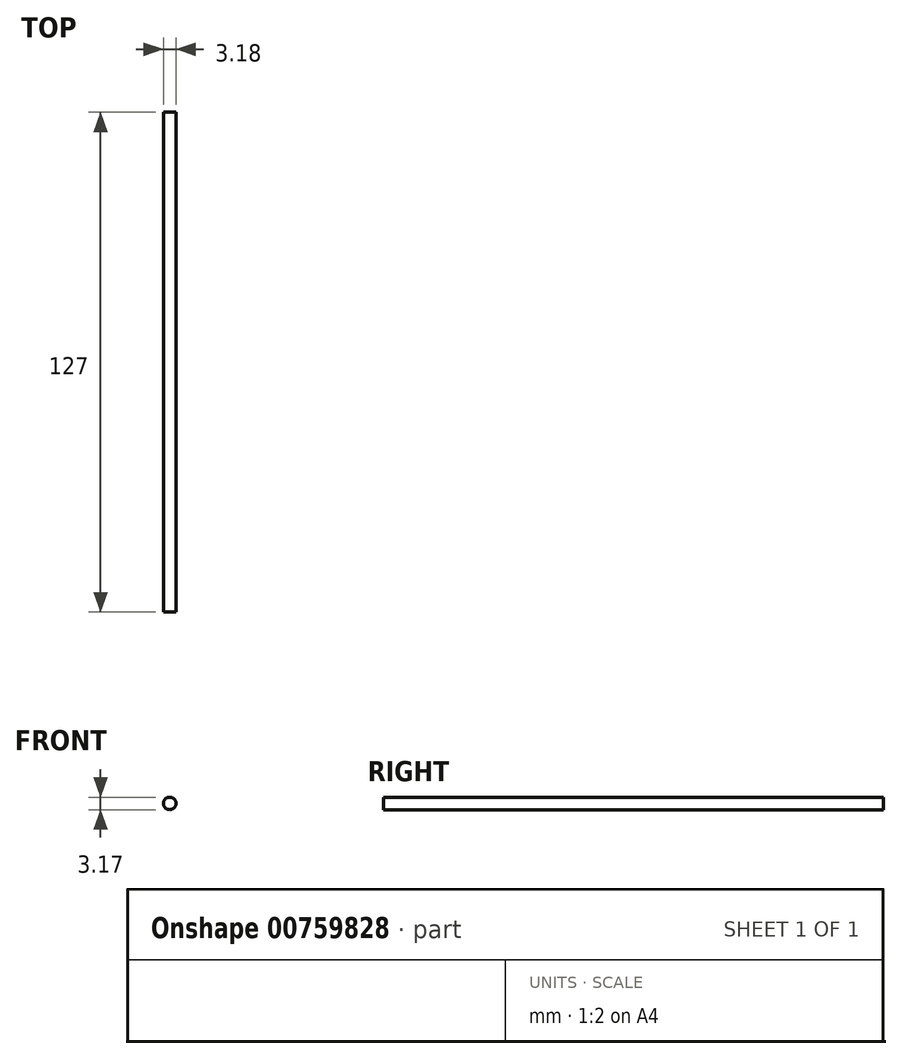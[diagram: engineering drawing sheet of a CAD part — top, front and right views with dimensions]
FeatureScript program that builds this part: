
annotation { "Feature Type Name" : "Feature", "Feature Type Description" : "" }
export const myFeature = defineFeature(function(context is Context, id is Id, definition is map)
    precondition{}
    {
        {
            var Q0;
            Q0=qCreatedBy(makeId("Front.planeOp"),FACE);
            var sketch = newSketch(context, id + "F0", { "sketchPlane" : qUnion([Q0])});
            skCircle(sketch, "E0", {"center": v(0, -0.87) * mm, "radius": 1.59 * mm});
            skSolve(sketch);
        }
        {
            var Q0;
            Q0=makeQuery(id+"F0.imprint","IMPRINT",FACE,{"disambiguationData":[TD([[makeQuery(id+"F0.imprint","IMPRINT",EDGE,{"derivedFrom":sQuery(id+"F0.wireOp",EDGE,"E0")}),1.0]])]});
            extrude(context, id + "F1", {"entities" : qUnion([Q0]), "depth" : 127 * mm, "offsetDistance" : 25.4 * mm});
        }
    });
